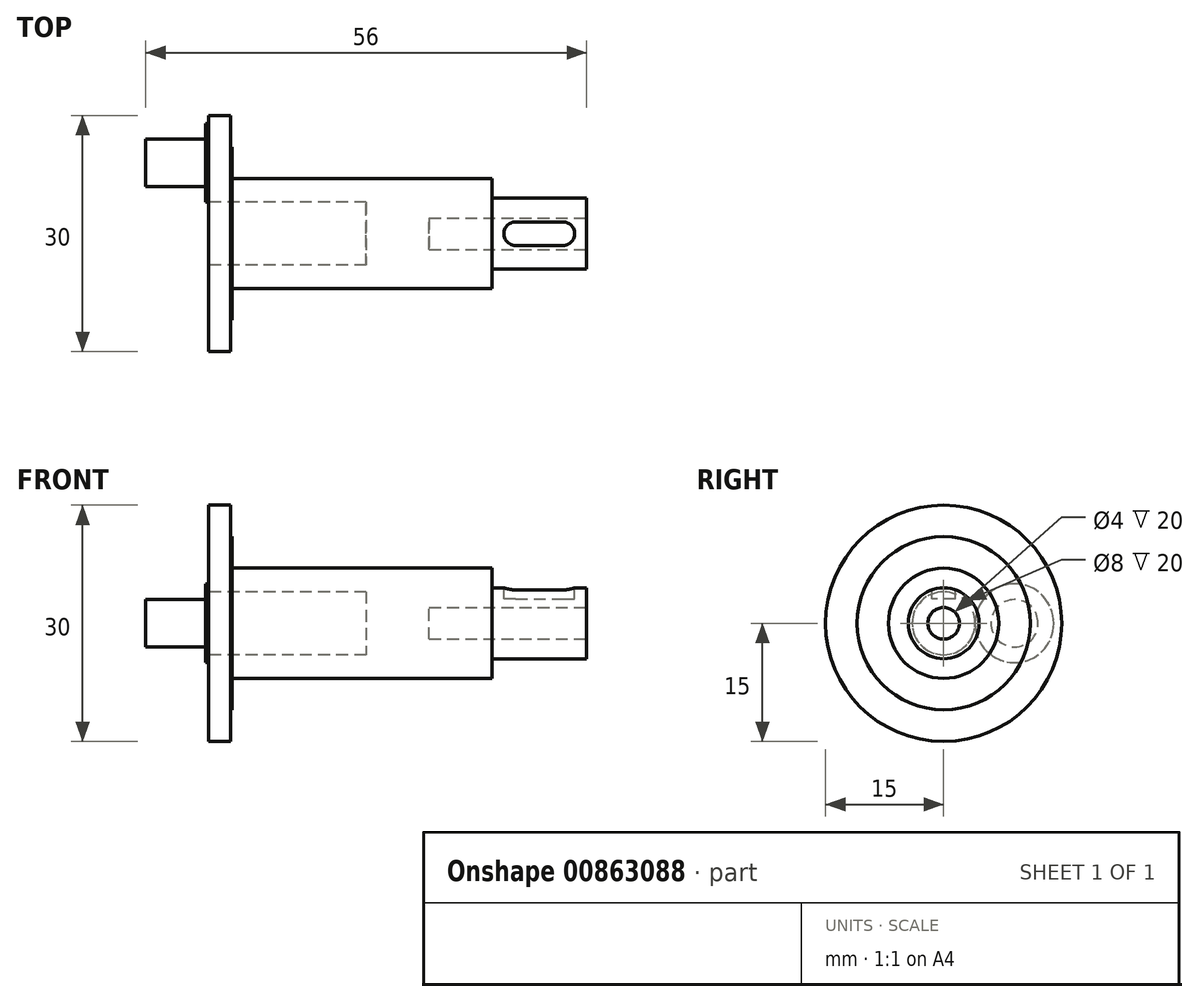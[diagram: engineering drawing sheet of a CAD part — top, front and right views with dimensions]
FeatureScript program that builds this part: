
annotation { "Feature Type Name" : "Feature", "Feature Type Description" : "" }
export const myFeature = defineFeature(function(context is Context, id is Id, definition is map)
    precondition{}
    {
        {
            var Q0;
            Q0=qCreatedBy(makeId("Front.planeOp"),FACE);
            var sketch = newSketch(context, id + "F0", { "sketchPlane" : qUnion([Q0])});
            skLineSegment(sketch, "E0", {"start": v(0, 0) * mm, "end": v(0, 15) * mm});
            skLineSegment(sketch, "E1", {"start": v(0, 15) * mm, "end": v(2.8, 15) * mm});
            skLineSegment(sketch, "E2", {"start": v(2.8, 15) * mm, "end": v(2.8, 11) * mm});
            skLineSegment(sketch, "E3", {"start": v(2.8, 11) * mm, "end": v(3, 11) * mm});
            skLineSegment(sketch, "E4", {"start": v(3, 11) * mm, "end": v(3, 7) * mm});
            skLineSegment(sketch, "E5", {"start": v(3, 7) * mm, "end": v(36, 7) * mm});
            skLineSegment(sketch, "E6", {"start": v(36, 7) * mm, "end": v(36, 4.5) * mm});
            skLineSegment(sketch, "E7", {"start": v(36, 4.5) * mm, "end": v(48, 4.5) * mm});
            skLineSegment(sketch, "E8", {"start": v(48, 4.5) * mm, "end": v(48, 0) * mm});
            skLineSegment(sketch, "E9", {"start": v(48, 0) * mm, "end": v(0, 0) * mm});
            skSolve(sketch);
        }
        {
            var Q0;
            Q0=makeQuery(id+"F0.imprint","IMPRINT",FACE,{"disambiguationData":[TD([[makeQuery(id+"F0.imprint","IMPRINT",EDGE,{"derivedFrom":sQuery(id+"F0.wireOp",EDGE,"E0")}),-1.0]])]});
            var Q1;
            Q1=sQuery(id+"F0.wireOp",EDGE,"E9");
            revolve(context, id + "F1", {"surfaceOperationType" : NewSurfaceOperationType.NEW, "entities" : qUnion([Q0]), "axis" : qUnion([Q1]), "revolveType" : RevolveType.FULL});
        }
        {
            var Q0;
            Q0=makeQuery(id+"F1.opRevolve","SWEPT_FACE",FACE,{"disambiguationData":[OSD([sQuery(id+"F0.wireOp",EDGE,"E8")])]});
            var sketch = newSketch(context, id + "F2", { "sketchPlane" : qUnion([Q0])});
            skCircle(sketch, "E10", {"center": v(0, 0) * mm, "radius": 2 * mm});
            skSolve(sketch);
        }
        {
            var Q0;
            Q0=makeQuery(id+"F2.imprint","IMPRINT",FACE,{"disambiguationData":[TD([[makeQuery(id+"F2.imprint","IMPRINT",EDGE,{"derivedFrom":sQuery(id+"F2.wireOp",EDGE,"E10")}),1.0]])]});
            extrude(context, id + "F3", {"entities" : qUnion([Q0]), "operationType" : NewBodyOperationType.REMOVE, "oppositeDirection" : true, "depth" : 20 * mm, "offsetDistance" : 25 * mm});
        }
        {
            var Q0;
            Q0=makeQuery(id+"F1.opRevolve","SWEPT_FACE",FACE,{"disambiguationData":[OSD([sQuery(id+"F0.wireOp",EDGE,"E0")])]});
            var sketch = newSketch(context, id + "F4", { "sketchPlane" : qUnion([Q0])});
            skCircle(sketch, "E11", {"center": v(0, 0) * mm, "radius": 4 * mm});
            skSolve(sketch);
        }
        {
            var Q0;
            Q0=makeQuery(id+"F4.imprint","IMPRINT",FACE,{"disambiguationData":[TD([[makeQuery(id+"F4.imprint","IMPRINT",EDGE,{"derivedFrom":sQuery(id+"F4.wireOp",EDGE,"E11")}),1.0]])]});
            extrude(context, id + "F5", {"entities" : qUnion([Q0]), "operationType" : NewBodyOperationType.REMOVE, "oppositeDirection" : true, "depth" : 20 * mm, "offsetDistance" : 25 * mm});
        }
        {
            var Q0;
            Q0=qCreatedBy(makeId("Top.planeOp"),FACE);
            cPlane(context, id + "F6", {"entities" : qUnion([Q0]), "cplaneType" : CPlaneType.OFFSET, "offset" : 4.5 * mm, "width" : 150 * mm, "height" : 150 * mm});
        }
        {
            var Q0;
            Q0=qCreatedBy(id+"F6.planeOp",FACE);
            var sketch = newSketch(context, id + "F7", { "sketchPlane" : qUnion([Q0])});
            skLineSegment(sketch, "E12", {"start": v(39, 0) * mm, "end": v(45, 0) * mm, "construction": true});
            skArc(sketch, "E13.0.startCap", {"start": v(39, -1.5) * mm, "mid": v(37.5, 0) * mm, "end": v(39, 1.5) * mm});
            skArc(sketch, "E13.0.endCap", {"start": v(45, 1.5) * mm, "mid": v(46.5, 0) * mm, "end": v(45, -1.5) * mm});
            skLineSegment(sketch, "E13.0.left", {"start": v(39, 1.5) * mm, "end": v(45, 1.5) * mm});
            skLineSegment(sketch, "E13.0.right", {"start": v(39, -1.5) * mm, "end": v(45, -1.5) * mm});
            skSolve(sketch);
        }
        {
            var Q0;
            Q0 = qSketchRegion(id + "F7", true);
            extrude(context, id + "F8", {"entities" : qUnion([Q0]), "operationType" : NewBodyOperationType.REMOVE, "oppositeDirection" : true, "depth" : 1.4 * mm, "offsetDistance" : 25 * mm});
        }
        {
            var Q0;
            Q0=makeQuery(id+"F1.opRevolve","SWEPT_FACE",FACE,{"disambiguationData":[OSD([sQuery(id+"F0.wireOp",EDGE,"E0")])]});
            var sketch = newSketch(context, id + "F9", { "sketchPlane" : qUnion([Q0])});
            skCircle(sketch, "E14", {"center": v(-9, 0) * mm, "radius": 5 * mm});
            skCircle(sketch, "E15", {"center": v(-9, 0) * mm, "radius": 3 * mm});
            skSolve(sketch);
        }
        {
            var Q0;
            Q0=makeQuery(id+"F9.imprint","IMPRINT",FACE,{"disambiguationData":[TD([[makeQuery(id+"F9.imprint","IMPRINT",EDGE,{"derivedFrom":sQuery(id+"F9.wireOp",EDGE,"E15")}),1.0]])]});
            extrude(context, id + "F10", {"entities" : qUnion([Q0]), "operationType" : NewBodyOperationType.ADD, "depth" : 8 * mm, "offsetDistance" : 25 * mm});
        }
        {
            var Q0;
            Q0=makeQuery(id+"F9.imprint","IMPRINT",FACE,{"disambiguationData":[TD([[makeQuery(id+"F9.imprint","IMPRINT",EDGE,{"derivedFrom":sQuery(id+"F9.wireOp",EDGE,"E14")}),1.0]])]});
            extrude(context, id + "F11", {"entities" : qUnion([Q0]), "operationType" : NewBodyOperationType.ADD, "depth" : 0.4 * mm, "offsetDistance" : 25 * mm});
        }
    });
